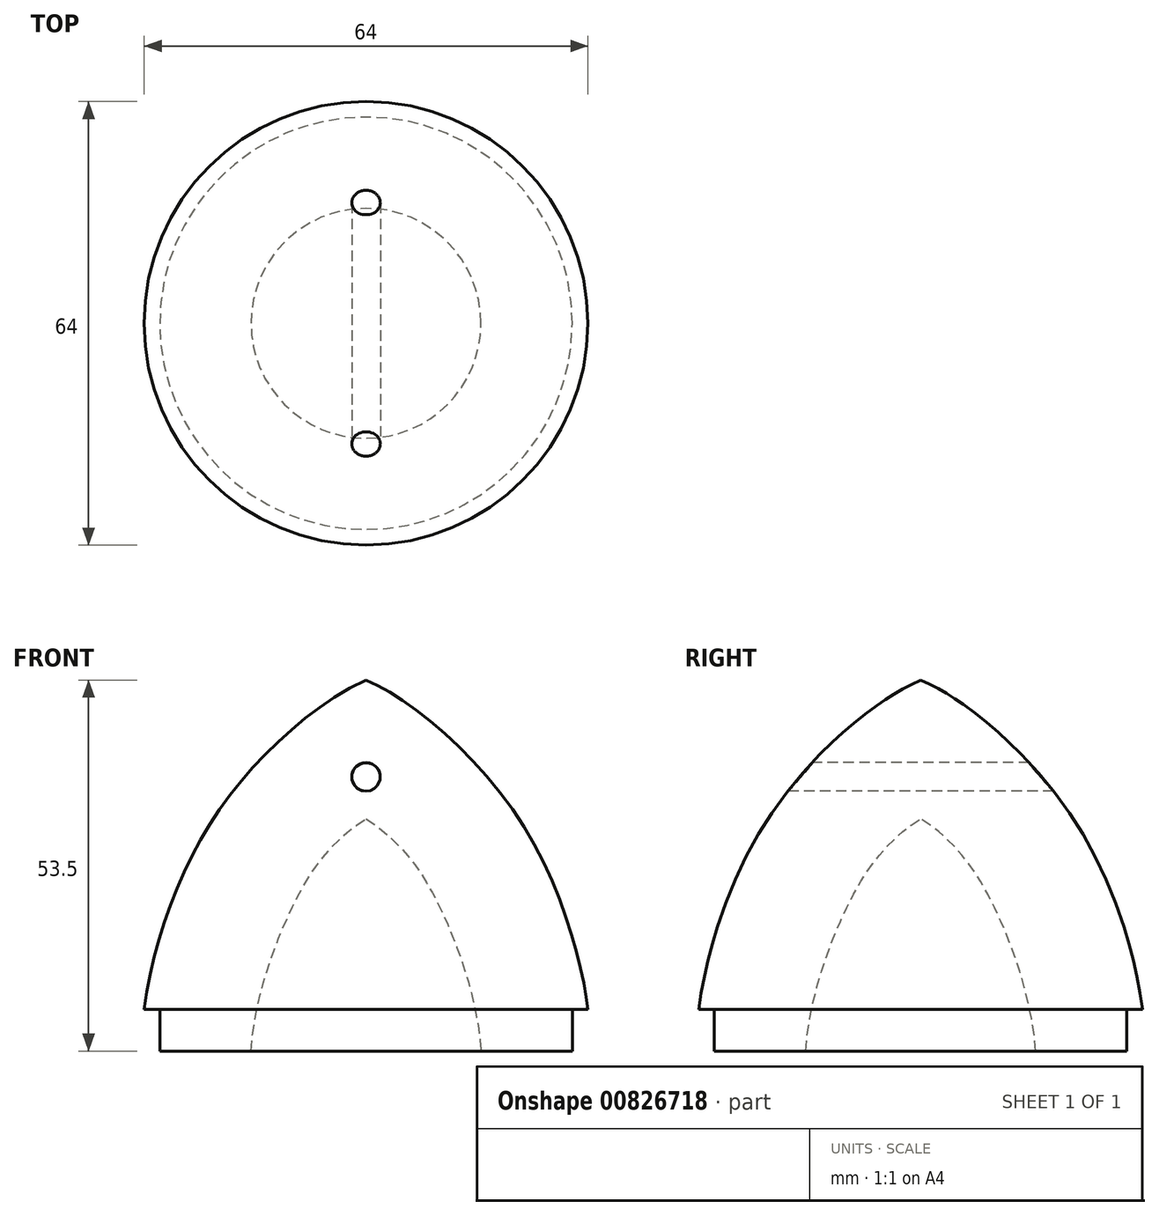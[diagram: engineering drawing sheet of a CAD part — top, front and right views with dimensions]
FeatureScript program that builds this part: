
annotation { "Feature Type Name" : "Feature", "Feature Type Description" : "" }
export const myFeature = defineFeature(function(context is Context, id is Id, definition is map)
    precondition{}
    {
        {
            var Q0;
            Q0=qCreatedBy(makeId("Front.planeOp"),FACE);
            var sketch = newSketch(context, id + "F0", { "sketchPlane" : qUnion([Q0])});
            skLineSegment(sketch, "E0", {"start": v(29.75, 117.78) * mm, "end": v(29.75, 123.78) * mm});
            skLineSegment(sketch, "E1", {"start": v(29.75, 123.78) * mm, "end": v(32, 123.78) * mm});
            skLineSegment(sketch, "E2", {"start": v(16.58, 117.78) * mm, "end": v(29.75, 117.78) * mm});
            skFitSpline(sketch, "E3", {"points": [v(0, 171.28) * mm, v(22.02, 151.32) * mm, v(32, 123.78) * mm], "startDerivative": vector(35.55, -14.44) * mm, "endDerivative": vector(4.6, -39.08) * mm});
            skFitSpline(sketch, "E4", {"points": [v(0, 151.28) * mm, v(11.15, 137.43) * mm, v(16.58, 117.78) * mm], "startDerivative": vector(33.2, -20.83) * mm, "endDerivative": vector(2.19, -36.07) * mm});
            skLineSegment(sketch, "E5", {"start": v(0, 171.28) * mm, "end": v(0, 151.28) * mm});
            skSolve(sketch);
        }
        {
            var Q0;
            Q0=qCreatedBy(makeId("Front.planeOp"),FACE);
            var sketch = newSketch(context, id + "F1", { "sketchPlane" : qUnion([Q0])});
            skLineSegment(sketch, "E6", {"start": v(0, 33.02) * mm, "end": v(0, 14.66) * mm});
            skSolve(sketch);
        }
        {
            var Q0;
            Q0=makeQuery(id+"F0.imprint","IMPRINT",FACE,{"disambiguationData":[TD([[makeQuery(id+"F0.imprint","IMPRINT",EDGE,{"derivedFrom":sQuery(id+"F0.wireOp",EDGE,"E0")}),1.0]])]});
            var Q1;
            Q1=sQuery(id+"F1.wireOp",EDGE,"E6");
            revolve(context, id + "F2", {"surfaceOperationType" : NewSurfaceOperationType.NEW, "entities" : qUnion([Q0]), "axis" : qUnion([Q1]), "revolveType" : RevolveType.FULL});
        }
        {
            var Q0;
            Q0=makeQuery(id+"F0.imprint","IMPRINT",FACE,{"disambiguationData":[TD([[makeQuery(id+"F0.imprint","IMPRINT",EDGE,{"derivedFrom":sQuery(id+"F0.wireOp",EDGE,"E0")}),1.0]])]});
            cPlane(context, id + "F3", {"entities" : qUnion([Q0]), "cplaneType" : CPlaneType.OFFSET, "offset" : 25 * mm, "width" : 150 * mm, "height" : 150 * mm});
        }
        {
            var Q0;
            Q0=qCreatedBy(id+"F3.planeOp",FACE);
            var sketch = newSketch(context, id + "F4", { "sketchPlane" : qUnion([Q0])});
            skCircle(sketch, "E7.0", {"center": v(0, 157.32) * mm, "radius": 2.06 * mm});
            skSolve(sketch);
        }
        {
            var Q0;
            Q0=makeQuery(id+"F4.imprint","IMPRINT",FACE,{"disambiguationData":[TD([[makeQuery(id+"F4.imprint","IMPRINT",EDGE,{"derivedFrom":sQuery(id+"F4.wireOp",EDGE,"E7.0")}),1.0]])]});
            extrude(context, id + "F5", {"entities" : qUnion([Q0]), "operationType" : NewBodyOperationType.REMOVE, "oppositeDirection" : true, "depth" : 47.2 * mm, "offsetDistance" : 25 * mm});
        }
    });
